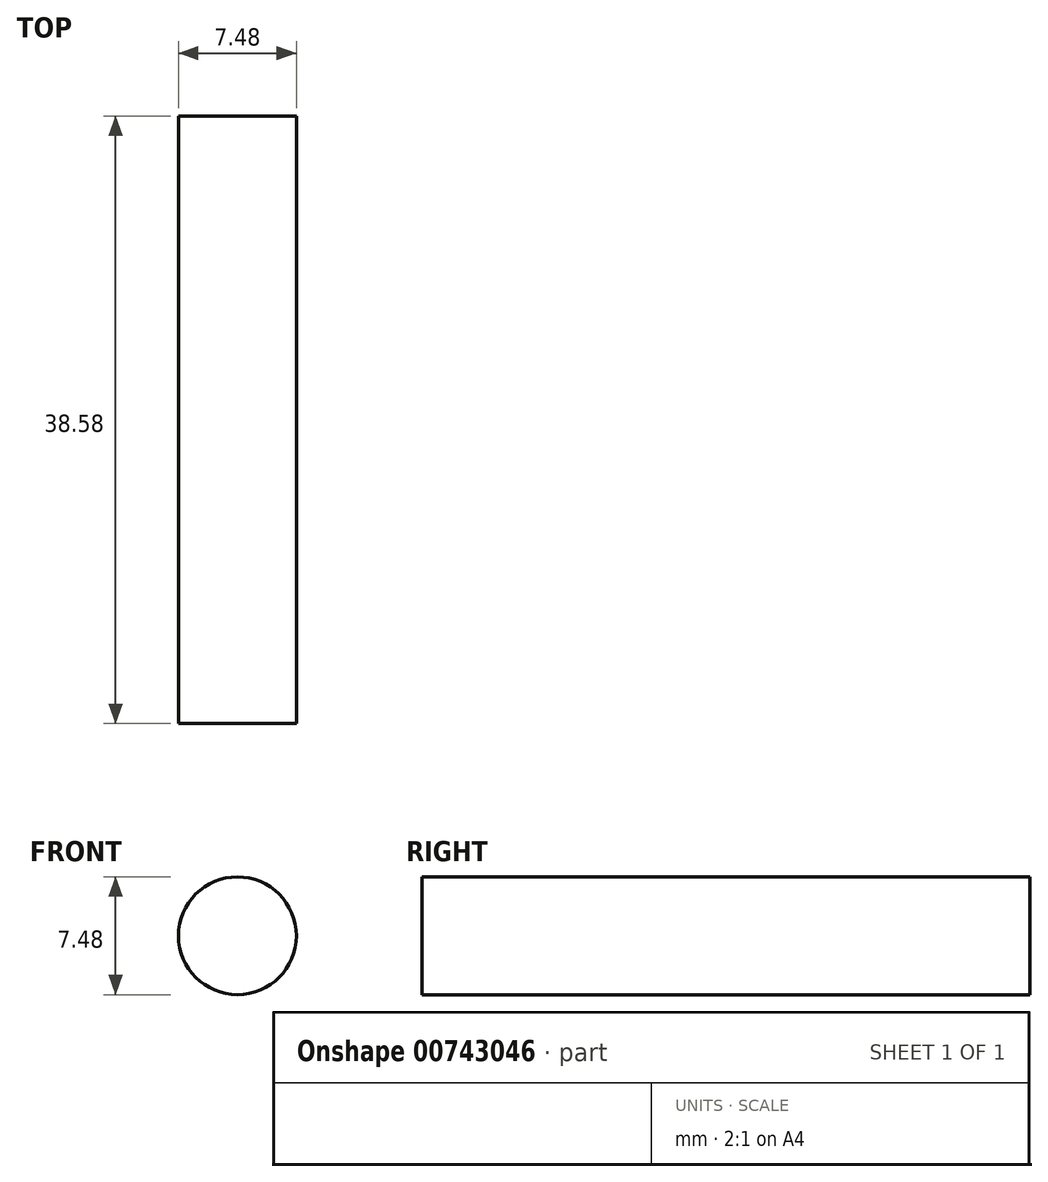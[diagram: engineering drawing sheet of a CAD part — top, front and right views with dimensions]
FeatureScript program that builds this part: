
annotation { "Feature Type Name" : "Feature", "Feature Type Description" : "" }
export const myFeature = defineFeature(function(context is Context, id is Id, definition is map)
    precondition{}
    {
        {
            var Q0;
            Q0=qCreatedBy(makeId("Front.planeOp"),FACE);
            var sketch = newSketch(context, id + "F0", { "sketchPlane" : qUnion([Q0])});
            skCircle(sketch, "E0", {"center": v(0, 0) * mm, "radius": 3.74 * mm});
            skSolve(sketch);
        }
        {
            var Q0;
            Q0 = qSketchRegion(id + "F0", true);
            extrude(context, id + "F1", {"entities" : qUnion([Q0]), "depth" : 38.58 * mm, "offsetDistance" : 25.4 * mm});
        }
    });
